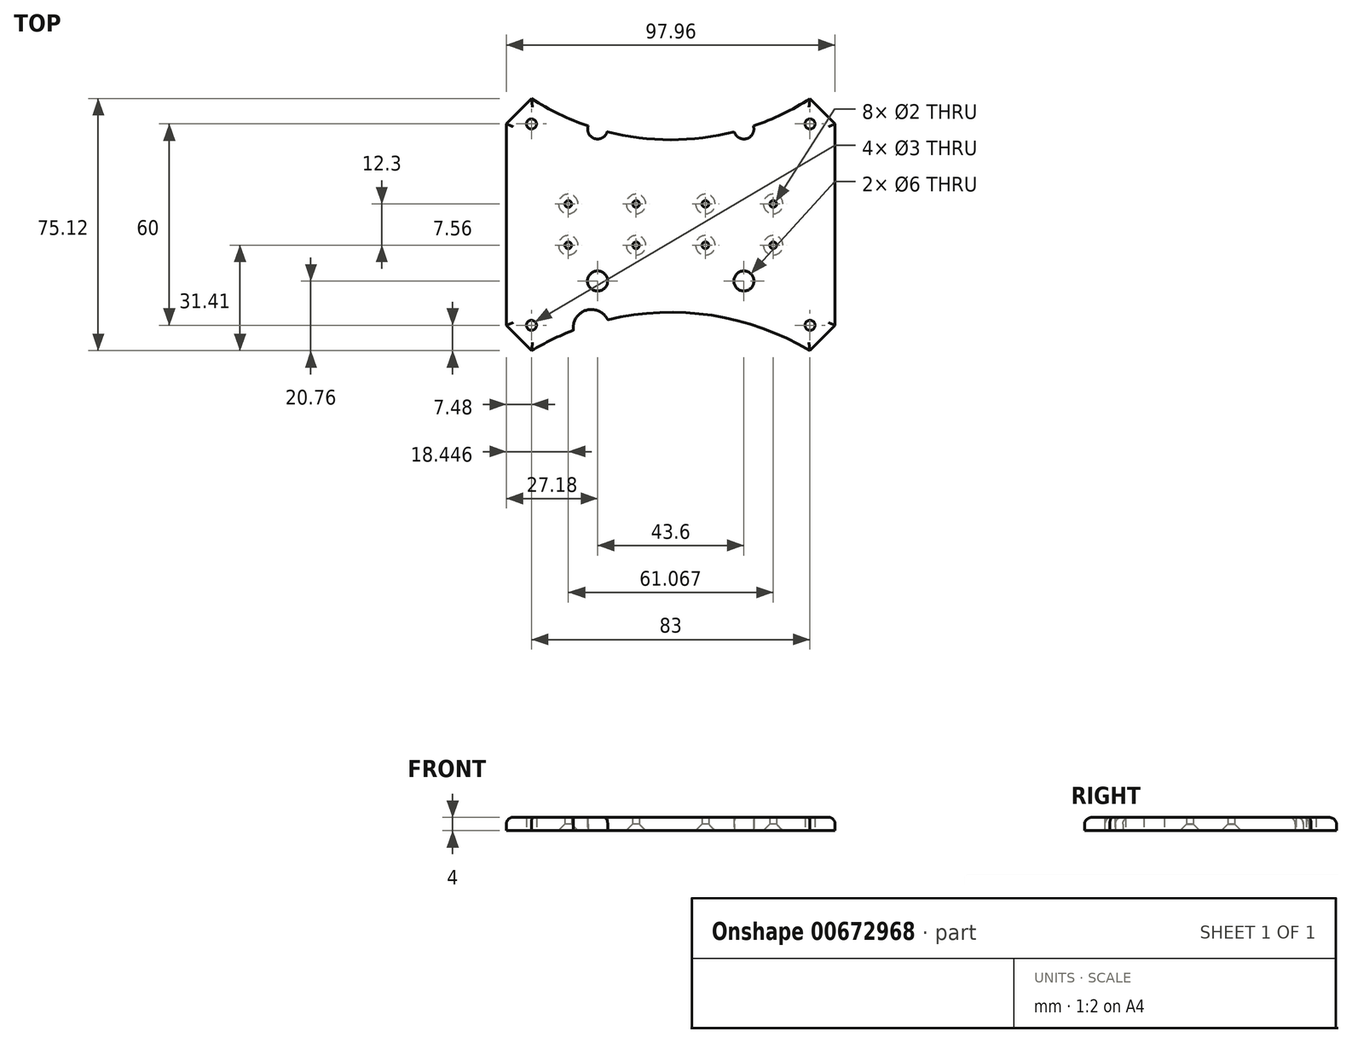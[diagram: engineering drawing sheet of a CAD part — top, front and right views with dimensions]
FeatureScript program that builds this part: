
annotation { "Feature Type Name" : "Feature", "Feature Type Description" : "" }
export const myFeature = defineFeature(function(context is Context, id is Id, definition is map)
    precondition{}
    {
        {
            var Q0;
            Q0=qCreatedBy(makeId("Top.planeOp"),FACE);
            var sketch = newSketch(context, id + "F0", { "sketchPlane" : qUnion([Q0])});
            skCircle(sketch, "E0", {"center": v(-41.5, 30) * mm, "radius": 1.5 * mm});
            skCircle(sketch, "E1", {"center": v(-41.5, -30) * mm, "radius": 1.5 * mm});
            skCircle(sketch, "E2.MirrorC", {"center": v(41.5, 30) * mm, "radius": 1.5 * mm});
            skCircle(sketch, "E3.MirrorC", {"center": v(41.5, -30) * mm, "radius": 1.5 * mm});
            skLineSegment(sketch, "E4", {"start": v(-41.5, 30) * mm, "end": v(-41.5, -30) * mm, "construction": true});
            skLineSegment(sketch, "E5", {"start": v(41.5, -30) * mm, "end": v(41.5, 30) * mm, "construction": true});
            skLineSegment(sketch, "E6", {"start": v(-41.5, 30) * mm, "end": v(41.5, 30) * mm, "construction": true});
            skLineSegment(sketch, "E7", {"start": v(-41.5, 30) * mm, "end": v(-48.98, 30) * mm, "construction": true});
            skLineSegment(sketch, "E8", {"start": v(-48.98, 30) * mm, "end": v(-48.98, -30) * mm, "construction": true});
            skLineSegment(sketch, "E9", {"start": v(-41.5, -30) * mm, "end": v(-48.98, -30) * mm, "construction": true});
            skLineSegment(sketch, "E10.MirrorCS", {"start": v(41.5, 30) * mm, "end": v(48.98, 30) * mm, "construction": true});
            skLineSegment(sketch, "E11.MirrorCS", {"start": v(48.98, 30) * mm, "end": v(48.98, -30) * mm, "construction": true});
            skLineSegment(sketch, "E12.MirrorCS", {"start": v(41.5, -30) * mm, "end": v(48.98, -30) * mm, "construction": true});
            skLineSegment(sketch, "E13", {"start": v(-48.98, -30) * mm, "end": v(-48.98, 30) * mm});
            skLineSegment(sketch, "E14", {"start": v(-41.5, 30) * mm, "end": v(-41.5, 37.56) * mm, "construction": true});
            skLineSegment(sketch, "E15", {"start": v(41.5, 30) * mm, "end": v(41.5, 37.56) * mm, "construction": true});
            skLineSegment(sketch, "E16.MirrorCS", {"start": v(41.5, -30) * mm, "end": v(41.5, -37.56) * mm, "construction": true});
            skLineSegment(sketch, "E17.MirrorCS", {"start": v(-41.5, -30) * mm, "end": v(-41.5, -37.56) * mm, "construction": true});
            skLineSegment(sketch, "E18", {"start": v(-48.98, 30) * mm, "end": v(-41.5, 37.56) * mm});
            skLineSegment(sketch, "E19", {"start": v(41.5, 37.56) * mm, "end": v(-41.5, 37.56) * mm});
            skLineSegment(sketch, "E20", {"start": v(41.5, 37.56) * mm, "end": v(48.98, 30) * mm});
            skLineSegment(sketch, "E21", {"start": v(48.98, -30) * mm, "end": v(48.98, 30) * mm});
            skLineSegment(sketch, "E22", {"start": v(48.98, -30) * mm, "end": v(41.5, -37.56) * mm});
            skLineSegment(sketch, "E23", {"start": v(41.5, -37.56) * mm, "end": v(-41.5, -37.56) * mm});
            skLineSegment(sketch, "E24", {"start": v(-41.5, -37.56) * mm, "end": v(-48.98, -30) * mm});
            skLineSegment(sketch, "E25", {"start": v(0, 0) * mm, "end": v(-20.43, 0) * mm, "construction": true});
            skLineSegment(sketch, "E26", {"start": v(0, 0) * mm, "end": v(20.43, 0) * mm, "construction": true});
            skLineSegment(sketch, "E27.bottom", {"start": v(-30.53, 6.15) * mm, "end": v(-10.33, 6.15) * mm});
            skLineSegment(sketch, "E27.top", {"start": v(-30.53, -6.15) * mm, "end": v(-10.33, -6.15) * mm});
            skLineSegment(sketch, "E27.left", {"start": v(-30.53, 6.15) * mm, "end": v(-30.53, -6.15) * mm});
            skLineSegment(sketch, "E27.right", {"start": v(-10.33, 6.15) * mm, "end": v(-10.33, -6.15) * mm});
            skPoint(sketch, "E27.middle", {"position": v(-20.43, 0) * mm});
            skCircle(sketch, "E28", {"center": v(-30.53, 6.15) * mm, "radius": 1 * mm});
            skCircle(sketch, "E29", {"center": v(-10.33, 6.15) * mm, "radius": 1 * mm});
            skCircle(sketch, "E30", {"center": v(-10.33, -6.15) * mm, "radius": 1 * mm});
            skCircle(sketch, "E31", {"center": v(-30.53, -6.15) * mm, "radius": 1 * mm});
            skLineSegment(sketch, "E32.MirrorCS", {"start": v(30.53, 6.15) * mm, "end": v(10.33, 6.15) * mm});
            skLineSegment(sketch, "E33.MirrorCS", {"start": v(10.33, 6.15) * mm, "end": v(10.33, -6.15) * mm});
            skCircle(sketch, "E34.MirrorC", {"center": v(10.33, 6.15) * mm, "radius": 1 * mm});
            skCircle(sketch, "E35.MirrorC", {"center": v(30.53, 6.15) * mm, "radius": 1 * mm});
            skCircle(sketch, "E36.MirrorC", {"center": v(10.33, -6.15) * mm, "radius": 1 * mm});
            skCircle(sketch, "E37.MirrorC", {"center": v(30.53, -6.15) * mm, "radius": 1 * mm});
            skLineSegment(sketch, "E38.MirrorCS", {"start": v(30.53, -6.15) * mm, "end": v(10.33, -6.15) * mm});
            skLineSegment(sketch, "E39.MirrorCS", {"start": v(30.53, 6.15) * mm, "end": v(30.53, -6.15) * mm});
            skLineSegment(sketch, "E40", {"start": v(-41.5, -30) * mm, "end": v(-21.8, -30) * mm, "construction": true});
            skLineSegment(sketch, "E41", {"start": v(-21.8, -30) * mm, "end": v(-21.8, -16.8) * mm, "construction": true});
            skCircle(sketch, "E42", {"center": v(-21.8, -16.8) * mm, "radius": 3 * mm});
            skCircle(sketch, "E43.MirrorC", {"center": v(21.8, -16.8) * mm, "radius": 3 * mm});
            skArc(sketch, "E44", {"start": v(-41.5, 37.56) * mm, "mid": v(0, 25.28) * mm, "end": v(41.5, 37.56) * mm});
            skArc(sketch, "E45", {"start": v(41.5, -37.56) * mm, "mid": v(0, -26.1) * mm, "end": v(-41.5, -37.56) * mm});
            skArc(sketch, "E46", {"start": v(-18.8, -28.3) * mm, "mid": v(-25.25, -25.52) * mm, "end": v(-29, -31.47) * mm});
            skArc(sketch, "E47", {"start": v(-18.94, 27.67) * mm, "mid": v(-22.65, 25.62) * mm, "end": v(-24.63, 29.37) * mm});
            skArc(sketch, "E48.MirrorCS", {"start": v(18.94, 27.67) * mm, "mid": v(22.65, 25.62) * mm, "end": v(24.63, 29.37) * mm});
            skSolve(sketch);
        }
        {
            var Q0;
            Q0=makeQuery(id+"F0.imprint","IMPRINT",FACE,{"disambiguationData":[TD([[makeQuery(id+"F0.imprint","IMPRINT",EDGE,{"derivedFrom":sQuery(id+"F0.wireOp",EDGE,"E0")}),-1.0]])]});
            var Q1;
            {var subQ5=sQuery(id+"F0.wireOp",EDGE,"E28");var subQ13=sQuery(id+"F0.wireOp",EDGE,"E27.bottom");var subQ14=makeQuery(id+"F0.imprint","INTERSECT",VERTEX,{"derivedFrom":[subQ13,subQ5]});Q1=makeQuery(id+"F0.imprint","IMPRINT",FACE,{"disambiguationData":[TD([[makeQuery(id+"F0.imprint","IMPRINT",EDGE,{"disambiguationData":[TD([[subQ14,-1.0]])],"derivedFrom":subQ13}),-1.0]])]});}
            var Q2;
            {var subQ6=sQuery(id+"F0.wireOp",EDGE,"E35.MirrorC");var subQ11=sQuery(id+"F0.wireOp",EDGE,"E32.MirrorCS");var subQ14=makeQuery(id+"F0.imprint","INTERSECT",VERTEX,{"derivedFrom":[subQ11,subQ6]});Q2=makeQuery(id+"F0.imprint","IMPRINT",FACE,{"disambiguationData":[TD([[makeQuery(id+"F0.imprint","IMPRINT",EDGE,{"disambiguationData":[TD([[subQ14,-1.0]])],"derivedFrom":subQ11}),1.0]])]});}
            var Q3;
            Q3=sQuery(id+"F0.wireOp",EDGE,"E0");
            var Q4;
            Q4=sQuery(id+"F0.wireOp",EDGE,"E24");
            var Q5;
            Q5=sQuery(id+"F0.wireOp",EDGE,"E18");
            var Q6;
            Q6=sQuery(id+"F0.wireOp",EDGE,"E22");
            var Q7;
            Q7=sQuery(id+"F0.wireOp",EDGE,"E1");
            var Q8;
            Q8=sQuery(id+"F0.wireOp",EDGE,"E19");
            var Q9;
            Q9=sQuery(id+"F0.wireOp",EDGE,"E2.MirrorC");
            var Q10;
            Q10=sQuery(id+"F0.wireOp",EDGE,"E23");
            var Q11;
            Q11=sQuery(id+"F0.wireOp",EDGE,"E20");
            var Q12;
            Q12=sQuery(id+"F0.wireOp",EDGE,"E3.MirrorC");
            var Q13;
            Q13=sQuery(id+"F0.wireOp",EDGE,"E21");
            var Q14;
            Q14=sQuery(id+"F0.wireOp",EDGE,"E13");
            extrude(context, id + "F1", {"entities" : qUnion([Q0, Q1, Q2]), "surfaceEntities" : qUnion([Q3, Q4, Q5, Q6, Q7, Q8, Q9, Q10, Q11, Q12, Q13, Q14]), "depth" : 4 * mm, "offsetDistance" : 25 * mm});
        }
        {
            var Q0;
            Q0=makeQuery(id+"F1.opExtrude","CAP_EDGE",EDGE,{"disambiguationData":[OSD([sQuery(id+"F0.wireOp",EDGE,"E37.MirrorC")])],"isStart":true});
            var Q1;
            Q1=makeQuery(id+"F1.opExtrude","CAP_EDGE",EDGE,{"disambiguationData":[OSD([sQuery(id+"F0.wireOp",EDGE,"E35.MirrorC")])],"isStart":true});
            var Q2;
            Q2=makeQuery(id+"F1.opExtrude","CAP_EDGE",EDGE,{"disambiguationData":[OSD([sQuery(id+"F0.wireOp",EDGE,"E34.MirrorC")])],"isStart":true});
            var Q3;
            Q3=makeQuery(id+"F1.opExtrude","CAP_EDGE",EDGE,{"disambiguationData":[OSD([sQuery(id+"F0.wireOp",EDGE,"E36.MirrorC")])],"isStart":true});
            var Q4;
            Q4=makeQuery(id+"F1.opExtrude","CAP_EDGE",EDGE,{"disambiguationData":[OSD([sQuery(id+"F0.wireOp",EDGE,"E30")])],"isStart":true});
            var Q5;
            Q5=makeQuery(id+"F1.opExtrude","CAP_EDGE",EDGE,{"disambiguationData":[OSD([sQuery(id+"F0.wireOp",EDGE,"E29")])],"isStart":true});
            var Q6;
            Q6=makeQuery(id+"F1.opExtrude","CAP_EDGE",EDGE,{"disambiguationData":[OSD([sQuery(id+"F0.wireOp",EDGE,"E28")])],"isStart":true});
            var Q7;
            Q7=makeQuery(id+"F1.opExtrude","CAP_EDGE",EDGE,{"disambiguationData":[OSD([sQuery(id+"F0.wireOp",EDGE,"E31")])],"isStart":true});
            chamfer(context, id + "F2", {"entities" : qUnion([Q0, Q1, Q2, Q3, Q4, Q5, Q6, Q7]), "width" : 1.9 * mm, "tangentPropagation" : true});
        }
        {
            var Q0;
            Q0=makeQuery(id+"F1.opExtrude","CAP_EDGE",EDGE,{"disambiguationData":[OSD([sQuery(id+"F0.wireOp",EDGE,"E13")])],"isStart":false});
            var Q1;
            Q1=makeQuery(id+"F1.opExtrude","CAP_EDGE",EDGE,{"disambiguationData":[OSD([sQuery(id+"F0.wireOp",EDGE,"E24")])],"isStart":false});
            var Q2;
            Q2=makeQuery(id+"F1.opExtrude","CAP_EDGE",EDGE,{"disambiguationData":[OSD([sQuery(id+"F0.wireOp",EDGE,"E45")])],"isStart":false});
            var Q3;
            Q3=makeQuery(id+"F1.opExtrude","CAP_EDGE",EDGE,{"disambiguationData":[OSD([sQuery(id+"F0.wireOp",EDGE,"E22")])],"isStart":false});
            var Q4;
            Q4=makeQuery(id+"F1.opExtrude","CAP_EDGE",EDGE,{"disambiguationData":[OSD([sQuery(id+"F0.wireOp",EDGE,"E21")])],"isStart":false});
            var Q5;
            Q5=makeQuery(id+"F1.opExtrude","CAP_EDGE",EDGE,{"disambiguationData":[OSD([sQuery(id+"F0.wireOp",EDGE,"E20")])],"isStart":false});
            var Q6;
            Q6=makeQuery(id+"F1.opExtrude","CAP_EDGE",EDGE,{"disambiguationData":[OSD([sQuery(id+"F0.wireOp",EDGE,"E44")])],"isStart":false});
            var Q7;
            Q7=makeQuery(id+"F1.opExtrude","CAP_EDGE",EDGE,{"disambiguationData":[OSD([sQuery(id+"F0.wireOp",EDGE,"E18")])],"isStart":false});
            fillet(context, id + "F3", {"entities" : qUnion([Q0, Q1, Q2, Q3, Q4, Q5, Q6, Q7]), "radius" : 2 * mm, "tangentPropagation" : true, "allowEdgeOverflow" : false});
        }
    });
